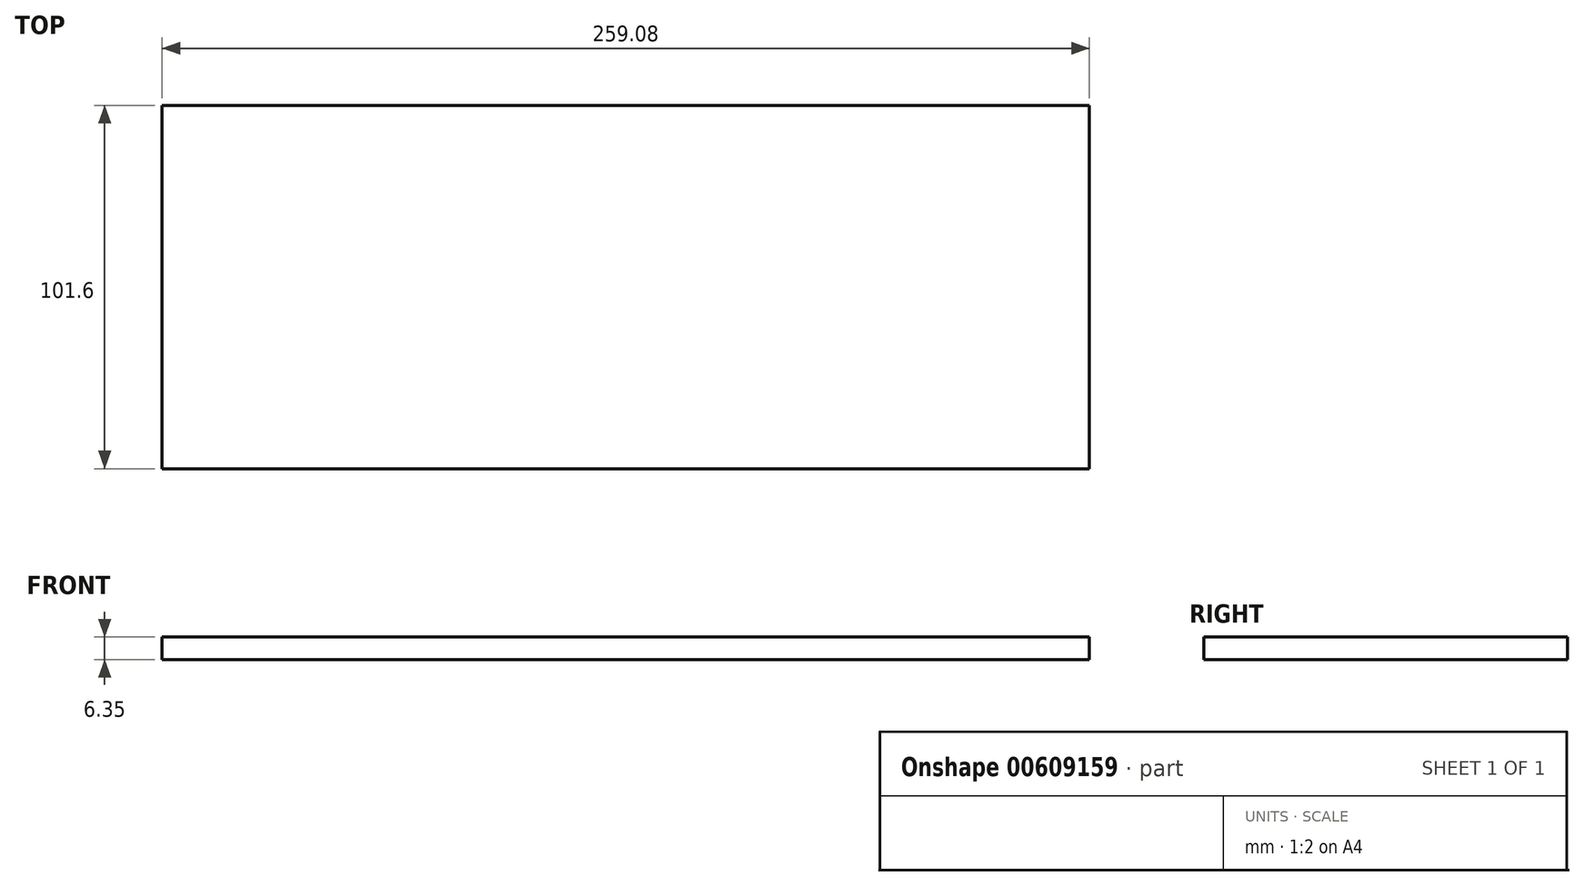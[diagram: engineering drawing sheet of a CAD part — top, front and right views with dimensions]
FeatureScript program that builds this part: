
annotation { "Feature Type Name" : "Feature", "Feature Type Description" : "" }
export const myFeature = defineFeature(function(context is Context, id is Id, definition is map)
    precondition{}
    {
        {
            var Q0;
            Q0=qCreatedBy(makeId("Top.planeOp"),FACE);
            var sketch = newSketch(context, id + "F0", { "sketchPlane" : qUnion([Q0])});
            skLineSegment(sketch, "E0.bottom", {"start": v(0, 0) * mm, "end": v(259.08, 0) * mm});
            skLineSegment(sketch, "E0.top", {"start": v(0, 101.6) * mm, "end": v(259.08, 101.6) * mm});
            skLineSegment(sketch, "E0.left", {"start": v(0, 0) * mm, "end": v(0, 101.6) * mm});
            skLineSegment(sketch, "E0.right", {"start": v(259.08, 0) * mm, "end": v(259.08, 101.6) * mm});
            skSolve(sketch);
        }
        {
            var Q0;
            Q0=makeQuery(id+"F0.imprint","IMPRINT",FACE,{"disambiguationData":[TD([[makeQuery(id+"F0.imprint","IMPRINT",EDGE,{"derivedFrom":sQuery(id+"F0.wireOp",EDGE,"E0.bottom")}),1.0]])]});
            extrude(context, id + "F1", {"entities" : qUnion([Q0]), "depth" : 6.35 * mm, "offsetDistance" : 25.4 * mm});
        }
    });
